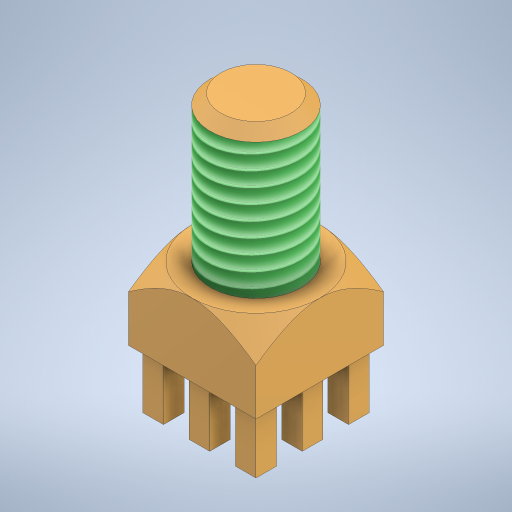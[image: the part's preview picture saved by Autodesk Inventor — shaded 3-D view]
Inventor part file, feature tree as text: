
AUTODESK INVENTOR PART (.ipt)
format: ipt  version: 2024 (Build 280153000, 153)  size: 370,688 bytes
history: native  units: mm
features: thread x1
ambient origin geometry x8: Origin, YZ Plane, XZ Plane, XY Plane, X Axis, Y Axis, Z Axis, Center Point
bodies: Volumenkörper1 (feature_tree)
feature tree (1):
  thread  "Gewinde1"  [1 undecoded]
note: 1 required parameter value undecoded (feature->parameter linkage not recoverable at this tier; creation-order binding heuristic only, values carry confidence <= 0.55)
